# Revit family: Hager-Orion-IP65-D300-Cl.I-Steel_encl-630A-PT-pt
name_source: partatom
category: Equipement électrique
units: mm (PartAtom-declared; Revit-internal decimal feet)

## family parameters
Configuration du panneau = Deux colonnes, circuits au sein
Cote de connecteur circulaire = Utiliser le diamètre
Couper avec des vides une fois chargée = Non
Hôte = Face
Partagée = Non
Point de calcul de pièce = Non
Type d'élément = Tableau de raccordement

## types (4) — shared parameters
Commentaires du type = Orion
EF000003 - Método de montagem = EV000384 - Montagem em superfície (gesso)
EF000007 - Cor = EV000270 - Cinzento
EF000116 - Número RAL = 7035
EF000118 - Com tampa de montagem = Oui
EF000339 - Tipo de difusor = EV004216 - Porta
EF000437 - Número de entradas de condutores = 2
EF001596 - Material do corpo = EV000179 - Aço
EF003532 - Adequado para uso no exterior = Non
EF004293 - Força de impacto = EV008784 - IK10
EF004464 - Tipo de porta = EV002646 - Único
EF005474 - Grau de proteção (IP) = EV006421 - IP65
EF006244 - Tampa/porta transparente = Non
EF006306 - Com fecho = Oui
EF007800 - Adequado para proteção contra raios = Non
EF008873 - Corrente nominal (In) = 630 A
EF009171 - Espessura do material da porta/tampa = 2 mm  [stored 0.00656168 ft]
EF009554 - Número de aberturas para placas de flange = 2
EF015940 - Tampa com libertação de sobrepressão = Non
Fabricant = Hager
HG000002 - Com porta ou tampa = Oui
HG000003 - Gama = Orion
HG000006 - Encastrado = Non
HG000009 - Porta dupla = Non
HG000010 - Portas assimétricas = Non
HG000023 - Recinto de secção dupla = Non
HG000024 - Altura da secção inferior = 800 mm  [stored 2.62467 ft]
HG000026 - Instalação no chão = Non
zero-valued in all types: EF000218 - Profundidade incorporada, EF002950 - Largura em número de módulos, EF004427 - Número de módulos, Elévation par défaut, HG000027 - Altura da Plinta

## per-type parameters (varying)
| type | EF000008 - Largura | EF000040 - Altura | EF000049 - Profundidade | EF000266 - Número de linhas | EF001088 - Extensão possível | EF001131 - Profundidade interior | EF001613 - Integridade do circuito | EF009170 - Espessura do material do invólucro | EF009212 - Tipo de tampa | HG000004 - Referência do Fabricante |
| Montagem em superfície (gesso) IP65 L600 A800 P300  - FL729L | 600 mm | 800 mm  [stored 2.62467 ft] | 300 mm | 1 | Oui | 200 mm  [stored 0.656168 ft] | EV000494 - Nenhum | 1 mm  [stored 0.00328084 ft] | EV000116 - Fechado | FL729L |
| Montagem em superfície (gesso) IP65 L600 A950 P300  - FL726L | 600 mm | 950 mm | 300 mm | 0 | Non | 300 mm |  | 2 mm  [stored 0.00656168 ft] | EV009916 - Com recuo | FL726L |
| Montagem em superfície (gesso) IP65 L800 A1250 P300  - FL730L | 800 mm  [stored 2.62467 ft] | 1250 mm  [stored 4.10105 ft] | 300 mm | 1 | Non | 300 mm |  | 2 mm  [stored 0.00656168 ft] | EV009916 - Com recuo | FL730L |
| Montagem em superfície (gesso) IP65 L800 A1250 P400  - FL731L | 800 mm  [stored 2.62467 ft] | 1250 mm  [stored 4.10105 ft] | 400 mm  [stored 1.31234 ft] | 0 | Non | 400 mm  [stored 1.31234 ft] |  | 2 mm  [stored 0.00656168 ft] | EV009916 - Com recuo | FL731L |

note: [stored X ft] marks values corroborated as IEEE doubles in the binary element streams (Revit-internal decimal feet)

## geometry (parser evidence)
native form markers: Sweep x7
no freeform markers — native parametric forms only
